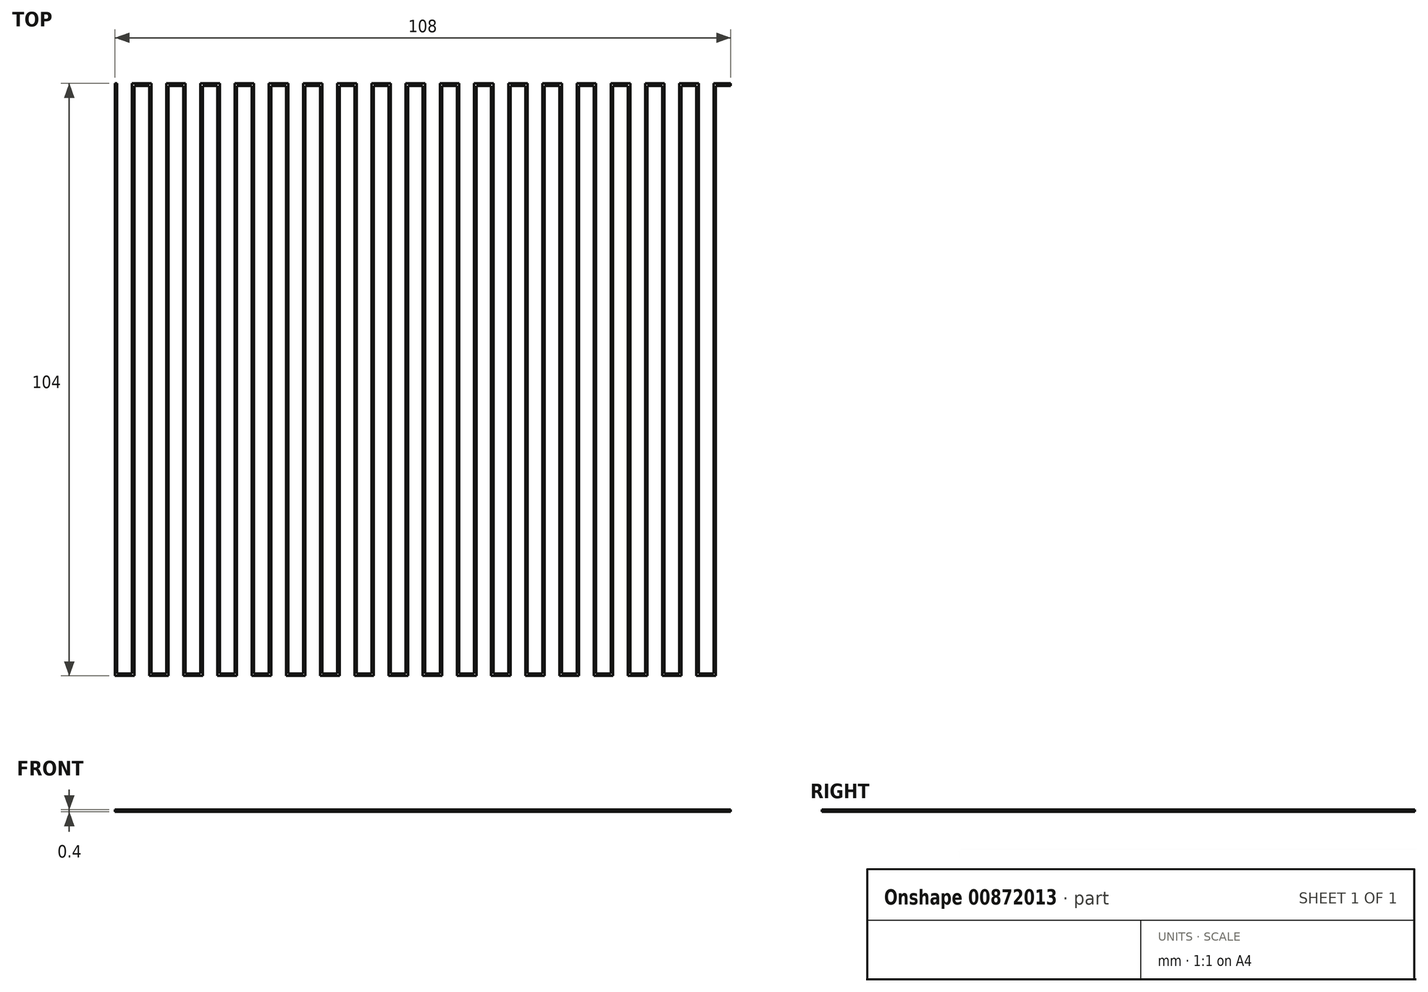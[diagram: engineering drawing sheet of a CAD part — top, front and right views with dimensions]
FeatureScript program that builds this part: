
annotation { "Feature Type Name" : "Feature", "Feature Type Description" : "" }
export const myFeature = defineFeature(function(context is Context, id is Id, definition is map)
    precondition{}
    {
        {
            var Q0;
            Q0=qCreatedBy(makeId("Top.planeOp"),FACE);
            var sketch = newSketch(context, id + "F0", { "sketchPlane" : qUnion([Q0])});
            skLineSegment(sketch, "E0.bottom", {"start": v(-52.6, 46.07) * mm, "end": v(-52.2, 46.07) * mm});
            skLineSegment(sketch, "E0.top", {"start": v(-52.6, -57.93) * mm, "end": v(-52.2, -57.93) * mm});
            skLineSegment(sketch, "E0.left", {"start": v(-52.6, 46.07) * mm, "end": v(-52.6, -57.93) * mm});
            skLineSegment(sketch, "E0.right", {"start": v(-52.2, 46.07) * mm, "end": v(-52.2, -57.93) * mm});
            skLineSegment(sketch, "E1.bottom", {"start": v(-52.6, -57.93) * mm, "end": v(-49.6, -57.93) * mm});
            skLineSegment(sketch, "E1.top", {"start": v(-52.6, -57.53) * mm, "end": v(-49.6, -57.53) * mm});
            skLineSegment(sketch, "E1.left", {"start": v(-52.6, -57.93) * mm, "end": v(-52.6, -57.53) * mm});
            skLineSegment(sketch, "E1.right", {"start": v(-49.6, -57.93) * mm, "end": v(-49.6, -57.53) * mm});
            skLineSegment(sketch, "E2.bottom", {"start": v(-49.6, -57.93) * mm, "end": v(-49.2, -57.93) * mm});
            skLineSegment(sketch, "E2.top", {"start": v(-49.6, 46.07) * mm, "end": v(-49.2, 46.07) * mm});
            skLineSegment(sketch, "E2.left", {"start": v(-49.6, -57.93) * mm, "end": v(-49.6, 46.07) * mm});
            skLineSegment(sketch, "E2.right", {"start": v(-49.2, -57.93) * mm, "end": v(-49.2, 46.07) * mm});
            skLineSegment(sketch, "E3.bottom", {"start": v(-49.6, 46.07) * mm, "end": v(-46.6, 46.07) * mm});
            skLineSegment(sketch, "E3.top", {"start": v(-49.6, 45.67) * mm, "end": v(-46.6, 45.67) * mm});
            skLineSegment(sketch, "E3.left", {"start": v(-49.6, 46.07) * mm, "end": v(-49.6, 45.67) * mm});
            skLineSegment(sketch, "E3.right", {"start": v(-46.6, 46.07) * mm, "end": v(-46.6, 45.67) * mm});
            skLineSegment(sketch, "E4.1.0.0", {"start": v(-46.2, 46.07) * mm, "end": v(-46.2, -57.93) * mm});
            skLineSegment(sketch, "E4.1.0.1", {"start": v(-46.6, 46.07) * mm, "end": v(-46.6, -57.93) * mm});
            skLineSegment(sketch, "E4.1.0.2", {"start": v(-43.2, -57.93) * mm, "end": v(-43.2, 46.07) * mm});
            skLineSegment(sketch, "E4.1.0.3", {"start": v(-43.6, -57.93) * mm, "end": v(-43.6, 46.07) * mm});
            skLineSegment(sketch, "E4.1.0.4", {"start": v(-43.6, 45.67) * mm, "end": v(-40.6, 45.67) * mm});
            skLineSegment(sketch, "E4.1.0.5", {"start": v(-46.6, 46.07) * mm, "end": v(-46.2, 46.07) * mm});
            skLineSegment(sketch, "E4.1.0.6", {"start": v(-43.6, 46.07) * mm, "end": v(-40.6, 46.07) * mm});
            skLineSegment(sketch, "E4.1.0.7", {"start": v(-40.6, 46.07) * mm, "end": v(-40.6, 45.67) * mm});
            skLineSegment(sketch, "E4.1.0.8", {"start": v(-46.6, -57.53) * mm, "end": v(-43.6, -57.53) * mm});
            skLineSegment(sketch, "E4.1.0.9", {"start": v(-46.6, -57.93) * mm, "end": v(-43.6, -57.93) * mm});
            skLineSegment(sketch, "E4.1.0.10", {"start": v(-46.6, -57.93) * mm, "end": v(-46.2, -57.93) * mm});
            skLineSegment(sketch, "E4.1.0.11", {"start": v(-46.6, -57.93) * mm, "end": v(-46.6, -57.53) * mm});
            skLineSegment(sketch, "E4.1.0.12", {"start": v(-43.6, -57.93) * mm, "end": v(-43.6, -57.53) * mm});
            skLineSegment(sketch, "E4.1.0.13", {"start": v(-43.6, -57.93) * mm, "end": v(-43.2, -57.93) * mm});
            skLineSegment(sketch, "E4.1.0.14", {"start": v(-43.6, 46.07) * mm, "end": v(-43.2, 46.07) * mm});
            skLineSegment(sketch, "E4.1.0.15", {"start": v(-43.6, 46.07) * mm, "end": v(-43.6, 45.67) * mm});
            skLineSegment(sketch, "E4.2.0.0", {"start": v(-40.2, 46.07) * mm, "end": v(-40.2, -57.93) * mm});
            skLineSegment(sketch, "E4.2.0.1", {"start": v(-40.6, 46.07) * mm, "end": v(-40.6, -57.93) * mm});
            skLineSegment(sketch, "E4.2.0.2", {"start": v(-37.2, -57.93) * mm, "end": v(-37.2, 46.07) * mm});
            skLineSegment(sketch, "E4.2.0.3", {"start": v(-37.6, -57.93) * mm, "end": v(-37.6, 46.07) * mm});
            skLineSegment(sketch, "E4.2.0.4", {"start": v(-37.6, 45.67) * mm, "end": v(-34.6, 45.67) * mm});
            skLineSegment(sketch, "E4.2.0.5", {"start": v(-40.6, 46.07) * mm, "end": v(-40.2, 46.07) * mm});
            skLineSegment(sketch, "E4.2.0.6", {"start": v(-37.6, 46.07) * mm, "end": v(-34.6, 46.07) * mm});
            skLineSegment(sketch, "E4.2.0.7", {"start": v(-34.6, 46.07) * mm, "end": v(-34.6, 45.67) * mm});
            skLineSegment(sketch, "E4.2.0.8", {"start": v(-40.6, -57.53) * mm, "end": v(-37.6, -57.53) * mm});
            skLineSegment(sketch, "E4.2.0.9", {"start": v(-40.6, -57.93) * mm, "end": v(-37.6, -57.93) * mm});
            skLineSegment(sketch, "E4.2.0.10", {"start": v(-40.6, -57.93) * mm, "end": v(-40.2, -57.93) * mm});
            skLineSegment(sketch, "E4.2.0.11", {"start": v(-40.6, -57.93) * mm, "end": v(-40.6, -57.53) * mm});
            skLineSegment(sketch, "E4.2.0.12", {"start": v(-37.6, -57.93) * mm, "end": v(-37.6, -57.53) * mm});
            skLineSegment(sketch, "E4.2.0.13", {"start": v(-37.6, -57.93) * mm, "end": v(-37.2, -57.93) * mm});
            skLineSegment(sketch, "E4.2.0.14", {"start": v(-37.6, 46.07) * mm, "end": v(-37.2, 46.07) * mm});
            skLineSegment(sketch, "E4.2.0.15", {"start": v(-37.6, 46.07) * mm, "end": v(-37.6, 45.67) * mm});
            skLineSegment(sketch, "E4.3.0.0", {"start": v(-34.2, 46.07) * mm, "end": v(-34.2, -57.93) * mm});
            skLineSegment(sketch, "E4.3.0.1", {"start": v(-34.6, 46.07) * mm, "end": v(-34.6, -57.93) * mm});
            skLineSegment(sketch, "E4.3.0.2", {"start": v(-31.2, -57.93) * mm, "end": v(-31.2, 46.07) * mm});
            skLineSegment(sketch, "E4.3.0.3", {"start": v(-31.6, -57.93) * mm, "end": v(-31.6, 46.07) * mm});
            skLineSegment(sketch, "E4.3.0.4", {"start": v(-31.6, 45.67) * mm, "end": v(-28.6, 45.67) * mm});
            skLineSegment(sketch, "E4.3.0.5", {"start": v(-34.6, 46.07) * mm, "end": v(-34.2, 46.07) * mm});
            skLineSegment(sketch, "E4.3.0.6", {"start": v(-31.6, 46.07) * mm, "end": v(-28.6, 46.07) * mm});
            skLineSegment(sketch, "E4.3.0.7", {"start": v(-28.6, 46.07) * mm, "end": v(-28.6, 45.67) * mm});
            skLineSegment(sketch, "E4.3.0.8", {"start": v(-34.6, -57.53) * mm, "end": v(-31.6, -57.53) * mm});
            skLineSegment(sketch, "E4.3.0.9", {"start": v(-34.6, -57.93) * mm, "end": v(-31.6, -57.93) * mm});
            skLineSegment(sketch, "E4.3.0.10", {"start": v(-34.6, -57.93) * mm, "end": v(-34.2, -57.93) * mm});
            skLineSegment(sketch, "E4.3.0.11", {"start": v(-34.6, -57.93) * mm, "end": v(-34.6, -57.53) * mm});
            skLineSegment(sketch, "E4.3.0.12", {"start": v(-31.6, -57.93) * mm, "end": v(-31.6, -57.53) * mm});
            skLineSegment(sketch, "E4.3.0.13", {"start": v(-31.6, -57.93) * mm, "end": v(-31.2, -57.93) * mm});
            skLineSegment(sketch, "E4.3.0.14", {"start": v(-31.6, 46.07) * mm, "end": v(-31.2, 46.07) * mm});
            skLineSegment(sketch, "E4.3.0.15", {"start": v(-31.6, 46.07) * mm, "end": v(-31.6, 45.67) * mm});
            skLineSegment(sketch, "E4.4.0.0", {"start": v(-28.2, 46.07) * mm, "end": v(-28.2, -57.93) * mm});
            skLineSegment(sketch, "E4.4.0.1", {"start": v(-28.6, 46.07) * mm, "end": v(-28.6, -57.93) * mm});
            skLineSegment(sketch, "E4.4.0.2", {"start": v(-25.2, -57.93) * mm, "end": v(-25.2, 46.07) * mm});
            skLineSegment(sketch, "E4.4.0.3", {"start": v(-25.6, -57.93) * mm, "end": v(-25.6, 46.07) * mm});
            skLineSegment(sketch, "E4.4.0.4", {"start": v(-25.6, 45.67) * mm, "end": v(-22.6, 45.67) * mm});
            skLineSegment(sketch, "E4.4.0.5", {"start": v(-28.6, 46.07) * mm, "end": v(-28.2, 46.07) * mm});
            skLineSegment(sketch, "E4.4.0.6", {"start": v(-25.6, 46.07) * mm, "end": v(-22.6, 46.07) * mm});
            skLineSegment(sketch, "E4.4.0.7", {"start": v(-22.6, 46.07) * mm, "end": v(-22.6, 45.67) * mm});
            skLineSegment(sketch, "E4.4.0.8", {"start": v(-28.6, -57.53) * mm, "end": v(-25.6, -57.53) * mm});
            skLineSegment(sketch, "E4.4.0.9", {"start": v(-28.6, -57.93) * mm, "end": v(-25.6, -57.93) * mm});
            skLineSegment(sketch, "E4.4.0.10", {"start": v(-28.6, -57.93) * mm, "end": v(-28.2, -57.93) * mm});
            skLineSegment(sketch, "E4.4.0.11", {"start": v(-28.6, -57.93) * mm, "end": v(-28.6, -57.53) * mm});
            skLineSegment(sketch, "E4.4.0.12", {"start": v(-25.6, -57.93) * mm, "end": v(-25.6, -57.53) * mm});
            skLineSegment(sketch, "E4.4.0.13", {"start": v(-25.6, -57.93) * mm, "end": v(-25.2, -57.93) * mm});
            skLineSegment(sketch, "E4.4.0.14", {"start": v(-25.6, 46.07) * mm, "end": v(-25.2, 46.07) * mm});
            skLineSegment(sketch, "E4.4.0.15", {"start": v(-25.6, 46.07) * mm, "end": v(-25.6, 45.67) * mm});
            skLineSegment(sketch, "E4.5.0.0", {"start": v(-22.2, 46.07) * mm, "end": v(-22.2, -57.93) * mm});
            skLineSegment(sketch, "E4.5.0.1", {"start": v(-22.6, 46.07) * mm, "end": v(-22.6, -57.93) * mm});
            skLineSegment(sketch, "E4.5.0.2", {"start": v(-19.2, -57.93) * mm, "end": v(-19.2, 46.07) * mm});
            skLineSegment(sketch, "E4.5.0.3", {"start": v(-19.6, -57.93) * mm, "end": v(-19.6, 46.07) * mm});
            skLineSegment(sketch, "E4.5.0.4", {"start": v(-19.6, 45.67) * mm, "end": v(-16.6, 45.67) * mm});
            skLineSegment(sketch, "E4.5.0.5", {"start": v(-22.6, 46.07) * mm, "end": v(-22.2, 46.07) * mm});
            skLineSegment(sketch, "E4.5.0.6", {"start": v(-19.6, 46.07) * mm, "end": v(-16.6, 46.07) * mm});
            skLineSegment(sketch, "E4.5.0.7", {"start": v(-16.6, 46.07) * mm, "end": v(-16.6, 45.67) * mm});
            skLineSegment(sketch, "E4.5.0.8", {"start": v(-22.6, -57.53) * mm, "end": v(-19.6, -57.53) * mm});
            skLineSegment(sketch, "E4.5.0.9", {"start": v(-22.6, -57.93) * mm, "end": v(-19.6, -57.93) * mm});
            skLineSegment(sketch, "E4.5.0.10", {"start": v(-22.6, -57.93) * mm, "end": v(-22.2, -57.93) * mm});
            skLineSegment(sketch, "E4.5.0.11", {"start": v(-22.6, -57.93) * mm, "end": v(-22.6, -57.53) * mm});
            skLineSegment(sketch, "E4.5.0.12", {"start": v(-19.6, -57.93) * mm, "end": v(-19.6, -57.53) * mm});
            skLineSegment(sketch, "E4.5.0.13", {"start": v(-19.6, -57.93) * mm, "end": v(-19.2, -57.93) * mm});
            skLineSegment(sketch, "E4.5.0.14", {"start": v(-19.6, 46.07) * mm, "end": v(-19.2, 46.07) * mm});
            skLineSegment(sketch, "E4.5.0.15", {"start": v(-19.6, 46.07) * mm, "end": v(-19.6, 45.67) * mm});
            skLineSegment(sketch, "E4.6.0.0", {"start": v(-16.2, 46.07) * mm, "end": v(-16.2, -57.93) * mm});
            skLineSegment(sketch, "E4.6.0.1", {"start": v(-16.6, 46.07) * mm, "end": v(-16.6, -57.93) * mm});
            skLineSegment(sketch, "E4.6.0.2", {"start": v(-13.2, -57.93) * mm, "end": v(-13.2, 46.07) * mm});
            skLineSegment(sketch, "E4.6.0.3", {"start": v(-13.6, -57.93) * mm, "end": v(-13.6, 46.07) * mm});
            skLineSegment(sketch, "E4.6.0.4", {"start": v(-13.6, 45.67) * mm, "end": v(-10.6, 45.67) * mm});
            skLineSegment(sketch, "E4.6.0.5", {"start": v(-16.6, 46.07) * mm, "end": v(-16.2, 46.07) * mm});
            skLineSegment(sketch, "E4.6.0.6", {"start": v(-13.6, 46.07) * mm, "end": v(-10.6, 46.07) * mm});
            skLineSegment(sketch, "E4.6.0.7", {"start": v(-10.6, 46.07) * mm, "end": v(-10.6, 45.67) * mm});
            skLineSegment(sketch, "E4.6.0.8", {"start": v(-16.6, -57.53) * mm, "end": v(-13.6, -57.53) * mm});
            skLineSegment(sketch, "E4.6.0.9", {"start": v(-16.6, -57.93) * mm, "end": v(-13.6, -57.93) * mm});
            skLineSegment(sketch, "E4.6.0.10", {"start": v(-16.6, -57.93) * mm, "end": v(-16.2, -57.93) * mm});
            skLineSegment(sketch, "E4.6.0.11", {"start": v(-16.6, -57.93) * mm, "end": v(-16.6, -57.53) * mm});
            skLineSegment(sketch, "E4.6.0.12", {"start": v(-13.6, -57.93) * mm, "end": v(-13.6, -57.53) * mm});
            skLineSegment(sketch, "E4.6.0.13", {"start": v(-13.6, -57.93) * mm, "end": v(-13.2, -57.93) * mm});
            skLineSegment(sketch, "E4.6.0.14", {"start": v(-13.6, 46.07) * mm, "end": v(-13.2, 46.07) * mm});
            skLineSegment(sketch, "E4.6.0.15", {"start": v(-13.6, 46.07) * mm, "end": v(-13.6, 45.67) * mm});
            skLineSegment(sketch, "E4.7.0.0", {"start": v(-10.2, 46.07) * mm, "end": v(-10.2, -57.93) * mm});
            skLineSegment(sketch, "E4.7.0.1", {"start": v(-10.6, 46.07) * mm, "end": v(-10.6, -57.93) * mm});
            skLineSegment(sketch, "E4.7.0.2", {"start": v(-7.2, -57.93) * mm, "end": v(-7.2, 46.07) * mm});
            skLineSegment(sketch, "E4.7.0.3", {"start": v(-7.6, -57.93) * mm, "end": v(-7.6, 46.07) * mm});
            skLineSegment(sketch, "E4.7.0.4", {"start": v(-7.6, 45.67) * mm, "end": v(-4.6, 45.67) * mm});
            skLineSegment(sketch, "E4.7.0.5", {"start": v(-10.6, 46.07) * mm, "end": v(-10.2, 46.07) * mm});
            skLineSegment(sketch, "E4.7.0.6", {"start": v(-7.6, 46.07) * mm, "end": v(-4.6, 46.07) * mm});
            skLineSegment(sketch, "E4.7.0.7", {"start": v(-4.6, 46.07) * mm, "end": v(-4.6, 45.67) * mm});
            skLineSegment(sketch, "E4.7.0.8", {"start": v(-10.6, -57.53) * mm, "end": v(-7.6, -57.53) * mm});
            skLineSegment(sketch, "E4.7.0.9", {"start": v(-10.6, -57.93) * mm, "end": v(-7.6, -57.93) * mm});
            skLineSegment(sketch, "E4.7.0.10", {"start": v(-10.6, -57.93) * mm, "end": v(-10.2, -57.93) * mm});
            skLineSegment(sketch, "E4.7.0.11", {"start": v(-10.6, -57.93) * mm, "end": v(-10.6, -57.53) * mm});
            skLineSegment(sketch, "E4.7.0.12", {"start": v(-7.6, -57.93) * mm, "end": v(-7.6, -57.53) * mm});
            skLineSegment(sketch, "E4.7.0.13", {"start": v(-7.6, -57.93) * mm, "end": v(-7.2, -57.93) * mm});
            skLineSegment(sketch, "E4.7.0.14", {"start": v(-7.6, 46.07) * mm, "end": v(-7.2, 46.07) * mm});
            skLineSegment(sketch, "E4.7.0.15", {"start": v(-7.6, 46.07) * mm, "end": v(-7.6, 45.67) * mm});
            skLineSegment(sketch, "E4.8.0.0", {"start": v(-4.2, 46.07) * mm, "end": v(-4.2, -57.93) * mm});
            skLineSegment(sketch, "E4.8.0.1", {"start": v(-4.6, 46.07) * mm, "end": v(-4.6, -57.93) * mm});
            skLineSegment(sketch, "E4.8.0.2", {"start": v(-1.2, -57.93) * mm, "end": v(-1.2, 46.07) * mm});
            skLineSegment(sketch, "E4.8.0.3", {"start": v(-1.6, -57.93) * mm, "end": v(-1.6, 46.07) * mm});
            skLineSegment(sketch, "E4.8.0.4", {"start": v(-1.6, 45.67) * mm, "end": v(1.4, 45.67) * mm});
            skLineSegment(sketch, "E4.8.0.5", {"start": v(-4.6, 46.07) * mm, "end": v(-4.2, 46.07) * mm});
            skLineSegment(sketch, "E4.8.0.6", {"start": v(-1.6, 46.07) * mm, "end": v(1.4, 46.07) * mm});
            skLineSegment(sketch, "E4.8.0.7", {"start": v(1.4, 46.07) * mm, "end": v(1.4, 45.67) * mm});
            skLineSegment(sketch, "E4.8.0.8", {"start": v(-4.6, -57.53) * mm, "end": v(-1.6, -57.53) * mm});
            skLineSegment(sketch, "E4.8.0.9", {"start": v(-4.6, -57.93) * mm, "end": v(-1.6, -57.93) * mm});
            skLineSegment(sketch, "E4.8.0.10", {"start": v(-4.6, -57.93) * mm, "end": v(-4.2, -57.93) * mm});
            skLineSegment(sketch, "E4.8.0.11", {"start": v(-4.6, -57.93) * mm, "end": v(-4.6, -57.53) * mm});
            skLineSegment(sketch, "E4.8.0.12", {"start": v(-1.6, -57.93) * mm, "end": v(-1.6, -57.53) * mm});
            skLineSegment(sketch, "E4.8.0.13", {"start": v(-1.6, -57.93) * mm, "end": v(-1.2, -57.93) * mm});
            skLineSegment(sketch, "E4.8.0.14", {"start": v(-1.6, 46.07) * mm, "end": v(-1.2, 46.07) * mm});
            skLineSegment(sketch, "E4.8.0.15", {"start": v(-1.6, 46.07) * mm, "end": v(-1.6, 45.67) * mm});
            skLineSegment(sketch, "E4.9.0.0", {"start": v(1.8, 46.07) * mm, "end": v(1.8, -57.93) * mm});
            skLineSegment(sketch, "E4.9.0.1", {"start": v(1.4, 46.07) * mm, "end": v(1.4, -57.93) * mm});
            skLineSegment(sketch, "E4.9.0.2", {"start": v(4.8, -57.93) * mm, "end": v(4.8, 46.07) * mm});
            skLineSegment(sketch, "E4.9.0.3", {"start": v(4.4, -57.93) * mm, "end": v(4.4, 46.07) * mm});
            skLineSegment(sketch, "E4.9.0.4", {"start": v(4.4, 45.67) * mm, "end": v(7.4, 45.67) * mm});
            skLineSegment(sketch, "E4.9.0.5", {"start": v(1.4, 46.07) * mm, "end": v(1.8, 46.07) * mm});
            skLineSegment(sketch, "E4.9.0.6", {"start": v(4.4, 46.07) * mm, "end": v(7.4, 46.07) * mm});
            skLineSegment(sketch, "E4.9.0.7", {"start": v(7.4, 46.07) * mm, "end": v(7.4, 45.67) * mm});
            skLineSegment(sketch, "E4.9.0.8", {"start": v(1.4, -57.53) * mm, "end": v(4.4, -57.53) * mm});
            skLineSegment(sketch, "E4.9.0.9", {"start": v(1.4, -57.93) * mm, "end": v(4.4, -57.93) * mm});
            skLineSegment(sketch, "E4.9.0.10", {"start": v(1.4, -57.93) * mm, "end": v(1.8, -57.93) * mm});
            skLineSegment(sketch, "E4.9.0.11", {"start": v(1.4, -57.93) * mm, "end": v(1.4, -57.53) * mm});
            skLineSegment(sketch, "E4.9.0.12", {"start": v(4.4, -57.93) * mm, "end": v(4.4, -57.53) * mm});
            skLineSegment(sketch, "E4.9.0.13", {"start": v(4.4, -57.93) * mm, "end": v(4.8, -57.93) * mm});
            skLineSegment(sketch, "E4.9.0.14", {"start": v(4.4, 46.07) * mm, "end": v(4.8, 46.07) * mm});
            skLineSegment(sketch, "E4.9.0.15", {"start": v(4.4, 46.07) * mm, "end": v(4.4, 45.67) * mm});
            skLineSegment(sketch, "E4.10.0.0", {"start": v(7.8, 46.07) * mm, "end": v(7.8, -57.93) * mm});
            skLineSegment(sketch, "E4.10.0.1", {"start": v(7.4, 46.07) * mm, "end": v(7.4, -57.93) * mm});
            skLineSegment(sketch, "E4.10.0.2", {"start": v(10.8, -57.93) * mm, "end": v(10.8, 46.07) * mm});
            skLineSegment(sketch, "E4.10.0.3", {"start": v(10.4, -57.93) * mm, "end": v(10.4, 46.07) * mm});
            skLineSegment(sketch, "E4.10.0.4", {"start": v(10.4, 45.67) * mm, "end": v(13.4, 45.67) * mm});
            skLineSegment(sketch, "E4.10.0.5", {"start": v(7.4, 46.07) * mm, "end": v(7.8, 46.07) * mm});
            skLineSegment(sketch, "E4.10.0.6", {"start": v(10.4, 46.07) * mm, "end": v(13.4, 46.07) * mm});
            skLineSegment(sketch, "E4.10.0.7", {"start": v(13.4, 46.07) * mm, "end": v(13.4, 45.67) * mm});
            skLineSegment(sketch, "E4.10.0.8", {"start": v(7.4, -57.53) * mm, "end": v(10.4, -57.53) * mm});
            skLineSegment(sketch, "E4.10.0.9", {"start": v(7.4, -57.93) * mm, "end": v(10.4, -57.93) * mm});
            skLineSegment(sketch, "E4.10.0.10", {"start": v(7.4, -57.93) * mm, "end": v(7.8, -57.93) * mm});
            skLineSegment(sketch, "E4.10.0.11", {"start": v(7.4, -57.93) * mm, "end": v(7.4, -57.53) * mm});
            skLineSegment(sketch, "E4.10.0.12", {"start": v(10.4, -57.93) * mm, "end": v(10.4, -57.53) * mm});
            skLineSegment(sketch, "E4.10.0.13", {"start": v(10.4, -57.93) * mm, "end": v(10.8, -57.93) * mm});
            skLineSegment(sketch, "E4.10.0.14", {"start": v(10.4, 46.07) * mm, "end": v(10.8, 46.07) * mm});
            skLineSegment(sketch, "E4.10.0.15", {"start": v(10.4, 46.07) * mm, "end": v(10.4, 45.67) * mm});
            skLineSegment(sketch, "E4.11.0.0", {"start": v(13.8, 46.07) * mm, "end": v(13.8, -57.93) * mm});
            skLineSegment(sketch, "E4.11.0.1", {"start": v(13.4, 46.07) * mm, "end": v(13.4, -57.93) * mm});
            skLineSegment(sketch, "E4.11.0.2", {"start": v(16.8, -57.93) * mm, "end": v(16.8, 46.07) * mm});
            skLineSegment(sketch, "E4.11.0.3", {"start": v(16.4, -57.93) * mm, "end": v(16.4, 46.07) * mm});
            skLineSegment(sketch, "E4.11.0.4", {"start": v(16.4, 45.67) * mm, "end": v(19.4, 45.67) * mm});
            skLineSegment(sketch, "E4.11.0.5", {"start": v(13.4, 46.07) * mm, "end": v(13.8, 46.07) * mm});
            skLineSegment(sketch, "E4.11.0.6", {"start": v(16.4, 46.07) * mm, "end": v(19.4, 46.07) * mm});
            skLineSegment(sketch, "E4.11.0.7", {"start": v(19.4, 46.07) * mm, "end": v(19.4, 45.67) * mm});
            skLineSegment(sketch, "E4.11.0.8", {"start": v(13.4, -57.53) * mm, "end": v(16.4, -57.53) * mm});
            skLineSegment(sketch, "E4.11.0.9", {"start": v(13.4, -57.93) * mm, "end": v(16.4, -57.93) * mm});
            skLineSegment(sketch, "E4.11.0.10", {"start": v(13.4, -57.93) * mm, "end": v(13.8, -57.93) * mm});
            skLineSegment(sketch, "E4.11.0.11", {"start": v(13.4, -57.93) * mm, "end": v(13.4, -57.53) * mm});
            skLineSegment(sketch, "E4.11.0.12", {"start": v(16.4, -57.93) * mm, "end": v(16.4, -57.53) * mm});
            skLineSegment(sketch, "E4.11.0.13", {"start": v(16.4, -57.93) * mm, "end": v(16.8, -57.93) * mm});
            skLineSegment(sketch, "E4.11.0.14", {"start": v(16.4, 46.07) * mm, "end": v(16.8, 46.07) * mm});
            skLineSegment(sketch, "E4.11.0.15", {"start": v(16.4, 46.07) * mm, "end": v(16.4, 45.67) * mm});
            skLineSegment(sketch, "E4.12.0.0", {"start": v(19.8, 46.07) * mm, "end": v(19.8, -57.93) * mm});
            skLineSegment(sketch, "E4.12.0.1", {"start": v(19.4, 46.07) * mm, "end": v(19.4, -57.93) * mm});
            skLineSegment(sketch, "E4.12.0.2", {"start": v(22.8, -57.93) * mm, "end": v(22.8, 46.07) * mm});
            skLineSegment(sketch, "E4.12.0.3", {"start": v(22.4, -57.93) * mm, "end": v(22.4, 46.07) * mm});
            skLineSegment(sketch, "E4.12.0.4", {"start": v(22.4, 45.67) * mm, "end": v(25.4, 45.67) * mm});
            skLineSegment(sketch, "E4.12.0.5", {"start": v(19.4, 46.07) * mm, "end": v(19.8, 46.07) * mm});
            skLineSegment(sketch, "E4.12.0.6", {"start": v(22.4, 46.07) * mm, "end": v(25.4, 46.07) * mm});
            skLineSegment(sketch, "E4.12.0.7", {"start": v(25.4, 46.07) * mm, "end": v(25.4, 45.67) * mm});
            skLineSegment(sketch, "E4.12.0.8", {"start": v(19.4, -57.53) * mm, "end": v(22.4, -57.53) * mm});
            skLineSegment(sketch, "E4.12.0.9", {"start": v(19.4, -57.93) * mm, "end": v(22.4, -57.93) * mm});
            skLineSegment(sketch, "E4.12.0.10", {"start": v(19.4, -57.93) * mm, "end": v(19.8, -57.93) * mm});
            skLineSegment(sketch, "E4.12.0.11", {"start": v(19.4, -57.93) * mm, "end": v(19.4, -57.53) * mm});
            skLineSegment(sketch, "E4.12.0.12", {"start": v(22.4, -57.93) * mm, "end": v(22.4, -57.53) * mm});
            skLineSegment(sketch, "E4.12.0.13", {"start": v(22.4, -57.93) * mm, "end": v(22.8, -57.93) * mm});
            skLineSegment(sketch, "E4.12.0.14", {"start": v(22.4, 46.07) * mm, "end": v(22.8, 46.07) * mm});
            skLineSegment(sketch, "E4.12.0.15", {"start": v(22.4, 46.07) * mm, "end": v(22.4, 45.67) * mm});
            skLineSegment(sketch, "E4.13.0.0", {"start": v(25.8, 46.07) * mm, "end": v(25.8, -57.93) * mm});
            skLineSegment(sketch, "E4.13.0.1", {"start": v(25.4, 46.07) * mm, "end": v(25.4, -57.93) * mm});
            skLineSegment(sketch, "E4.13.0.2", {"start": v(28.8, -57.93) * mm, "end": v(28.8, 46.07) * mm});
            skLineSegment(sketch, "E4.13.0.3", {"start": v(28.4, -57.93) * mm, "end": v(28.4, 46.07) * mm});
            skLineSegment(sketch, "E4.13.0.4", {"start": v(28.4, 45.67) * mm, "end": v(31.4, 45.67) * mm});
            skLineSegment(sketch, "E4.13.0.5", {"start": v(25.4, 46.07) * mm, "end": v(25.8, 46.07) * mm});
            skLineSegment(sketch, "E4.13.0.6", {"start": v(28.4, 46.07) * mm, "end": v(31.4, 46.07) * mm});
            skLineSegment(sketch, "E4.13.0.7", {"start": v(31.4, 46.07) * mm, "end": v(31.4, 45.67) * mm});
            skLineSegment(sketch, "E4.13.0.8", {"start": v(25.4, -57.53) * mm, "end": v(28.4, -57.53) * mm});
            skLineSegment(sketch, "E4.13.0.9", {"start": v(25.4, -57.93) * mm, "end": v(28.4, -57.93) * mm});
            skLineSegment(sketch, "E4.13.0.10", {"start": v(25.4, -57.93) * mm, "end": v(25.8, -57.93) * mm});
            skLineSegment(sketch, "E4.13.0.11", {"start": v(25.4, -57.93) * mm, "end": v(25.4, -57.53) * mm});
            skLineSegment(sketch, "E4.13.0.12", {"start": v(28.4, -57.93) * mm, "end": v(28.4, -57.53) * mm});
            skLineSegment(sketch, "E4.13.0.13", {"start": v(28.4, -57.93) * mm, "end": v(28.8, -57.93) * mm});
            skLineSegment(sketch, "E4.13.0.14", {"start": v(28.4, 46.07) * mm, "end": v(28.8, 46.07) * mm});
            skLineSegment(sketch, "E4.13.0.15", {"start": v(28.4, 46.07) * mm, "end": v(28.4, 45.67) * mm});
            skLineSegment(sketch, "E4.14.0.0", {"start": v(31.8, 46.07) * mm, "end": v(31.8, -57.93) * mm});
            skLineSegment(sketch, "E4.14.0.1", {"start": v(31.4, 46.07) * mm, "end": v(31.4, -57.93) * mm});
            skLineSegment(sketch, "E4.14.0.2", {"start": v(34.8, -57.93) * mm, "end": v(34.8, 46.07) * mm});
            skLineSegment(sketch, "E4.14.0.3", {"start": v(34.4, -57.93) * mm, "end": v(34.4, 46.07) * mm});
            skLineSegment(sketch, "E4.14.0.4", {"start": v(34.4, 45.67) * mm, "end": v(37.4, 45.67) * mm});
            skLineSegment(sketch, "E4.14.0.5", {"start": v(31.4, 46.07) * mm, "end": v(31.8, 46.07) * mm});
            skLineSegment(sketch, "E4.14.0.6", {"start": v(34.4, 46.07) * mm, "end": v(37.4, 46.07) * mm});
            skLineSegment(sketch, "E4.14.0.7", {"start": v(37.4, 46.07) * mm, "end": v(37.4, 45.67) * mm});
            skLineSegment(sketch, "E4.14.0.8", {"start": v(31.4, -57.53) * mm, "end": v(34.4, -57.53) * mm});
            skLineSegment(sketch, "E4.14.0.9", {"start": v(31.4, -57.93) * mm, "end": v(34.4, -57.93) * mm});
            skLineSegment(sketch, "E4.14.0.10", {"start": v(31.4, -57.93) * mm, "end": v(31.8, -57.93) * mm});
            skLineSegment(sketch, "E4.14.0.11", {"start": v(31.4, -57.93) * mm, "end": v(31.4, -57.53) * mm});
            skLineSegment(sketch, "E4.14.0.12", {"start": v(34.4, -57.93) * mm, "end": v(34.4, -57.53) * mm});
            skLineSegment(sketch, "E4.14.0.13", {"start": v(34.4, -57.93) * mm, "end": v(34.8, -57.93) * mm});
            skLineSegment(sketch, "E4.14.0.14", {"start": v(34.4, 46.07) * mm, "end": v(34.8, 46.07) * mm});
            skLineSegment(sketch, "E4.14.0.15", {"start": v(34.4, 46.07) * mm, "end": v(34.4, 45.67) * mm});
            skLineSegment(sketch, "E4.15.0.0", {"start": v(37.8, 46.07) * mm, "end": v(37.8, -57.93) * mm});
            skLineSegment(sketch, "E4.15.0.1", {"start": v(37.4, 46.07) * mm, "end": v(37.4, -57.93) * mm});
            skLineSegment(sketch, "E4.15.0.2", {"start": v(40.8, -57.93) * mm, "end": v(40.8, 46.07) * mm});
            skLineSegment(sketch, "E4.15.0.3", {"start": v(40.4, -57.93) * mm, "end": v(40.4, 46.07) * mm});
            skLineSegment(sketch, "E4.15.0.4", {"start": v(40.4, 45.67) * mm, "end": v(43.4, 45.67) * mm});
            skLineSegment(sketch, "E4.15.0.5", {"start": v(37.4, 46.07) * mm, "end": v(37.8, 46.07) * mm});
            skLineSegment(sketch, "E4.15.0.6", {"start": v(40.4, 46.07) * mm, "end": v(43.4, 46.07) * mm});
            skLineSegment(sketch, "E4.15.0.7", {"start": v(43.4, 46.07) * mm, "end": v(43.4, 45.67) * mm});
            skLineSegment(sketch, "E4.15.0.8", {"start": v(37.4, -57.53) * mm, "end": v(40.4, -57.53) * mm});
            skLineSegment(sketch, "E4.15.0.9", {"start": v(37.4, -57.93) * mm, "end": v(40.4, -57.93) * mm});
            skLineSegment(sketch, "E4.15.0.10", {"start": v(37.4, -57.93) * mm, "end": v(37.8, -57.93) * mm});
            skLineSegment(sketch, "E4.15.0.11", {"start": v(37.4, -57.93) * mm, "end": v(37.4, -57.53) * mm});
            skLineSegment(sketch, "E4.15.0.12", {"start": v(40.4, -57.93) * mm, "end": v(40.4, -57.53) * mm});
            skLineSegment(sketch, "E4.15.0.13", {"start": v(40.4, -57.93) * mm, "end": v(40.8, -57.93) * mm});
            skLineSegment(sketch, "E4.15.0.14", {"start": v(40.4, 46.07) * mm, "end": v(40.8, 46.07) * mm});
            skLineSegment(sketch, "E4.15.0.15", {"start": v(40.4, 46.07) * mm, "end": v(40.4, 45.67) * mm});
            skLineSegment(sketch, "E4.16.0.0", {"start": v(43.8, 46.07) * mm, "end": v(43.8, -57.93) * mm});
            skLineSegment(sketch, "E4.16.0.1", {"start": v(43.4, 46.07) * mm, "end": v(43.4, -57.93) * mm});
            skLineSegment(sketch, "E4.16.0.2", {"start": v(46.8, -57.93) * mm, "end": v(46.8, 46.07) * mm});
            skLineSegment(sketch, "E4.16.0.3", {"start": v(46.4, -57.93) * mm, "end": v(46.4, 46.07) * mm});
            skLineSegment(sketch, "E4.16.0.4", {"start": v(46.4, 45.67) * mm, "end": v(49.4, 45.67) * mm});
            skLineSegment(sketch, "E4.16.0.5", {"start": v(43.4, 46.07) * mm, "end": v(43.8, 46.07) * mm});
            skLineSegment(sketch, "E4.16.0.6", {"start": v(46.4, 46.07) * mm, "end": v(49.4, 46.07) * mm});
            skLineSegment(sketch, "E4.16.0.7", {"start": v(49.4, 46.07) * mm, "end": v(49.4, 45.67) * mm});
            skLineSegment(sketch, "E4.16.0.8", {"start": v(43.4, -57.53) * mm, "end": v(46.4, -57.53) * mm});
            skLineSegment(sketch, "E4.16.0.9", {"start": v(43.4, -57.93) * mm, "end": v(46.4, -57.93) * mm});
            skLineSegment(sketch, "E4.16.0.10", {"start": v(43.4, -57.93) * mm, "end": v(43.8, -57.93) * mm});
            skLineSegment(sketch, "E4.16.0.11", {"start": v(43.4, -57.93) * mm, "end": v(43.4, -57.53) * mm});
            skLineSegment(sketch, "E4.16.0.12", {"start": v(46.4, -57.93) * mm, "end": v(46.4, -57.53) * mm});
            skLineSegment(sketch, "E4.16.0.13", {"start": v(46.4, -57.93) * mm, "end": v(46.8, -57.93) * mm});
            skLineSegment(sketch, "E4.16.0.14", {"start": v(46.4, 46.07) * mm, "end": v(46.8, 46.07) * mm});
            skLineSegment(sketch, "E4.16.0.15", {"start": v(46.4, 46.07) * mm, "end": v(46.4, 45.67) * mm});
            skLineSegment(sketch, "E4.17.0.0", {"start": v(49.8, 46.07) * mm, "end": v(49.8, -57.93) * mm});
            skLineSegment(sketch, "E4.17.0.1", {"start": v(49.4, 46.07) * mm, "end": v(49.4, -57.93) * mm});
            skLineSegment(sketch, "E4.17.0.2", {"start": v(52.8, -57.93) * mm, "end": v(52.8, 46.07) * mm});
            skLineSegment(sketch, "E4.17.0.3", {"start": v(52.4, -57.93) * mm, "end": v(52.4, 46.07) * mm});
            skLineSegment(sketch, "E4.17.0.4", {"start": v(52.4, 45.67) * mm, "end": v(55.4, 45.67) * mm});
            skLineSegment(sketch, "E4.17.0.5", {"start": v(49.4, 46.07) * mm, "end": v(49.8, 46.07) * mm});
            skLineSegment(sketch, "E4.17.0.6", {"start": v(52.4, 46.07) * mm, "end": v(55.4, 46.07) * mm});
            skLineSegment(sketch, "E4.17.0.7", {"start": v(55.4, 46.07) * mm, "end": v(55.4, 45.67) * mm});
            skLineSegment(sketch, "E4.17.0.8", {"start": v(49.4, -57.53) * mm, "end": v(52.4, -57.53) * mm});
            skLineSegment(sketch, "E4.17.0.9", {"start": v(49.4, -57.93) * mm, "end": v(52.4, -57.93) * mm});
            skLineSegment(sketch, "E4.17.0.10", {"start": v(49.4, -57.93) * mm, "end": v(49.8, -57.93) * mm});
            skLineSegment(sketch, "E4.17.0.11", {"start": v(49.4, -57.93) * mm, "end": v(49.4, -57.53) * mm});
            skLineSegment(sketch, "E4.17.0.12", {"start": v(52.4, -57.93) * mm, "end": v(52.4, -57.53) * mm});
            skLineSegment(sketch, "E4.17.0.13", {"start": v(52.4, -57.93) * mm, "end": v(52.8, -57.93) * mm});
            skLineSegment(sketch, "E4.17.0.14", {"start": v(52.4, 46.07) * mm, "end": v(52.8, 46.07) * mm});
            skLineSegment(sketch, "E4.17.0.15", {"start": v(52.4, 46.07) * mm, "end": v(52.4, 45.67) * mm});
            skLineSegment(sketch, "E4.direction1", {"start": v(-52.6, -57.93) * mm, "end": v(-46.6, -57.93) * mm, "construction": true});
            skSolve(sketch);
        }
        {
            var Q0;
            {var subQ0=sQuery(id+"F0.wireOp",EDGE,"E4.17.0.6");var subQ1=sQuery(id+"F0.wireOp",EDGE,"E4.17.0.2");var subQ2=makeQuery(id+"F0.imprint","INTERSECT",VERTEX,{"derivedFrom":[subQ1,subQ0]});var subQ5=makeQuery(id+"F0.imprint","IMPRINT",EDGE,{"disambiguationData":[TD([[subQ2,1.0]])],"derivedFrom":subQ1});var subQ12=sQuery(id+"F0.wireOp",EDGE,"E4.17.0.13");var subQ13=sQuery(id+"F0.wireOp",EDGE,"E4.17.0.9");var subQ16=sQuery(id+"F0.wireOp",EDGE,"E4.17.0.0");var subQ17=makeQuery(id+"F0.imprint","INTERSECT",VERTEX,{"derivedFrom":[subQ16,subQ13]});var subQ19=makeQuery(id+"F0.imprint","IMPRINT",EDGE,{"disambiguationData":[TD([[subQ17,1.0]])],"derivedFrom":subQ16});var subQ25=sQuery(id+"F0.wireOp",EDGE,"E4.16.0.7");var subQ28=makeQuery(id+"F0.imprint","IMPRINT",EDGE,{"derivedFrom":subQ25});var subQ29=sQuery(id+"F0.wireOp",EDGE,"E4.16.0.6");var subQ30=sQuery(id+"F0.wireOp",EDGE,"E4.16.0.2");var subQ31=makeQuery(id+"F0.imprint","INTERSECT",VERTEX,{"derivedFrom":[subQ30,subQ29]});var subQ33=makeQuery(id+"F0.imprint","IMPRINT",EDGE,{"disambiguationData":[TD([[subQ31,1.0]])],"derivedFrom":subQ30});var subQ40=sQuery(id+"F0.wireOp",EDGE,"E4.16.0.13");var subQ41=sQuery(id+"F0.wireOp",EDGE,"E4.16.0.9");var subQ44=sQuery(id+"F0.wireOp",EDGE,"E4.16.0.0");var subQ45=makeQuery(id+"F0.imprint","INTERSECT",VERTEX,{"derivedFrom":[subQ44,subQ41]});var subQ47=makeQuery(id+"F0.imprint","IMPRINT",EDGE,{"disambiguationData":[TD([[subQ45,1.0]])],"derivedFrom":subQ44});var subQ53=sQuery(id+"F0.wireOp",EDGE,"E4.15.0.7");var subQ56=makeQuery(id+"F0.imprint","IMPRINT",EDGE,{"derivedFrom":subQ53});var subQ57=sQuery(id+"F0.wireOp",EDGE,"E4.15.0.6");var subQ58=sQuery(id+"F0.wireOp",EDGE,"E4.15.0.2");var subQ59=makeQuery(id+"F0.imprint","INTERSECT",VERTEX,{"derivedFrom":[subQ58,subQ57]});var subQ61=makeQuery(id+"F0.imprint","IMPRINT",EDGE,{"disambiguationData":[TD([[subQ59,1.0]])],"derivedFrom":subQ58});var subQ68=sQuery(id+"F0.wireOp",EDGE,"E4.15.0.13");var subQ69=sQuery(id+"F0.wireOp",EDGE,"E4.15.0.9");var subQ72=sQuery(id+"F0.wireOp",EDGE,"E4.15.0.0");var subQ73=makeQuery(id+"F0.imprint","INTERSECT",VERTEX,{"derivedFrom":[subQ72,subQ69]});var subQ75=makeQuery(id+"F0.imprint","IMPRINT",EDGE,{"disambiguationData":[TD([[subQ73,1.0]])],"derivedFrom":subQ72});var subQ81=sQuery(id+"F0.wireOp",EDGE,"E4.14.0.7");var subQ84=makeQuery(id+"F0.imprint","IMPRINT",EDGE,{"derivedFrom":subQ81});var subQ85=sQuery(id+"F0.wireOp",EDGE,"E4.14.0.6");var subQ86=sQuery(id+"F0.wireOp",EDGE,"E4.14.0.2");var subQ87=makeQuery(id+"F0.imprint","INTERSECT",VERTEX,{"derivedFrom":[subQ86,subQ85]});var subQ89=makeQuery(id+"F0.imprint","IMPRINT",EDGE,{"disambiguationData":[TD([[subQ87,1.0]])],"derivedFrom":subQ86});var subQ96=sQuery(id+"F0.wireOp",EDGE,"E4.14.0.13");var subQ97=sQuery(id+"F0.wireOp",EDGE,"E4.14.0.9");var subQ100=sQuery(id+"F0.wireOp",EDGE,"E4.14.0.0");var subQ101=makeQuery(id+"F0.imprint","INTERSECT",VERTEX,{"derivedFrom":[subQ100,subQ97]});var subQ103=makeQuery(id+"F0.imprint","IMPRINT",EDGE,{"disambiguationData":[TD([[subQ101,1.0]])],"derivedFrom":subQ100});var subQ109=sQuery(id+"F0.wireOp",EDGE,"E4.13.0.7");var subQ112=makeQuery(id+"F0.imprint","IMPRINT",EDGE,{"derivedFrom":subQ109});var subQ113=sQuery(id+"F0.wireOp",EDGE,"E4.13.0.6");var subQ114=sQuery(id+"F0.wireOp",EDGE,"E4.13.0.2");var subQ115=makeQuery(id+"F0.imprint","INTERSECT",VERTEX,{"derivedFrom":[subQ114,subQ113]});var subQ117=makeQuery(id+"F0.imprint","IMPRINT",EDGE,{"disambiguationData":[TD([[subQ115,1.0]])],"derivedFrom":subQ114});var subQ124=sQuery(id+"F0.wireOp",EDGE,"E4.13.0.13");var subQ125=sQuery(id+"F0.wireOp",EDGE,"E4.13.0.9");var subQ128=sQuery(id+"F0.wireOp",EDGE,"E4.13.0.0");var subQ129=makeQuery(id+"F0.imprint","INTERSECT",VERTEX,{"derivedFrom":[subQ128,subQ125]});var subQ131=makeQuery(id+"F0.imprint","IMPRINT",EDGE,{"disambiguationData":[TD([[subQ129,1.0]])],"derivedFrom":subQ128});var subQ137=sQuery(id+"F0.wireOp",EDGE,"E4.12.0.7");var subQ140=makeQuery(id+"F0.imprint","IMPRINT",EDGE,{"derivedFrom":subQ137});var subQ141=sQuery(id+"F0.wireOp",EDGE,"E4.12.0.6");var subQ142=sQuery(id+"F0.wireOp",EDGE,"E4.12.0.2");var subQ143=makeQuery(id+"F0.imprint","INTERSECT",VERTEX,{"derivedFrom":[subQ142,subQ141]});var subQ145=makeQuery(id+"F0.imprint","IMPRINT",EDGE,{"disambiguationData":[TD([[subQ143,1.0]])],"derivedFrom":subQ142});var subQ152=sQuery(id+"F0.wireOp",EDGE,"E4.12.0.13");var subQ153=sQuery(id+"F0.wireOp",EDGE,"E4.12.0.9");var subQ156=sQuery(id+"F0.wireOp",EDGE,"E4.12.0.0");var subQ157=makeQuery(id+"F0.imprint","INTERSECT",VERTEX,{"derivedFrom":[subQ156,subQ153]});var subQ159=makeQuery(id+"F0.imprint","IMPRINT",EDGE,{"disambiguationData":[TD([[subQ157,1.0]])],"derivedFrom":subQ156});var subQ165=sQuery(id+"F0.wireOp",EDGE,"E4.11.0.7");var subQ168=makeQuery(id+"F0.imprint","IMPRINT",EDGE,{"derivedFrom":subQ165});var subQ169=sQuery(id+"F0.wireOp",EDGE,"E4.11.0.6");var subQ170=sQuery(id+"F0.wireOp",EDGE,"E4.11.0.2");var subQ171=makeQuery(id+"F0.imprint","INTERSECT",VERTEX,{"derivedFrom":[subQ170,subQ169]});var subQ173=makeQuery(id+"F0.imprint","IMPRINT",EDGE,{"disambiguationData":[TD([[subQ171,1.0]])],"derivedFrom":subQ170});var subQ180=sQuery(id+"F0.wireOp",EDGE,"E4.11.0.13");var subQ181=sQuery(id+"F0.wireOp",EDGE,"E4.11.0.9");var subQ184=sQuery(id+"F0.wireOp",EDGE,"E4.11.0.0");var subQ185=makeQuery(id+"F0.imprint","INTERSECT",VERTEX,{"derivedFrom":[subQ184,subQ181]});var subQ187=makeQuery(id+"F0.imprint","IMPRINT",EDGE,{"disambiguationData":[TD([[subQ185,1.0]])],"derivedFrom":subQ184});var subQ193=sQuery(id+"F0.wireOp",EDGE,"E4.10.0.7");var subQ196=makeQuery(id+"F0.imprint","IMPRINT",EDGE,{"derivedFrom":subQ193});var subQ197=sQuery(id+"F0.wireOp",EDGE,"E4.10.0.6");var subQ198=sQuery(id+"F0.wireOp",EDGE,"E4.10.0.2");var subQ199=makeQuery(id+"F0.imprint","INTERSECT",VERTEX,{"derivedFrom":[subQ198,subQ197]});var subQ201=makeQuery(id+"F0.imprint","IMPRINT",EDGE,{"disambiguationData":[TD([[subQ199,1.0]])],"derivedFrom":subQ198});var subQ208=sQuery(id+"F0.wireOp",EDGE,"E4.10.0.13");var subQ209=sQuery(id+"F0.wireOp",EDGE,"E4.10.0.9");var subQ212=sQuery(id+"F0.wireOp",EDGE,"E4.10.0.0");var subQ213=makeQuery(id+"F0.imprint","INTERSECT",VERTEX,{"derivedFrom":[subQ212,subQ209]});var subQ215=makeQuery(id+"F0.imprint","IMPRINT",EDGE,{"disambiguationData":[TD([[subQ213,1.0]])],"derivedFrom":subQ212});var subQ221=sQuery(id+"F0.wireOp",EDGE,"E4.9.0.7");var subQ224=makeQuery(id+"F0.imprint","IMPRINT",EDGE,{"derivedFrom":subQ221});var subQ225=sQuery(id+"F0.wireOp",EDGE,"E4.9.0.6");var subQ226=sQuery(id+"F0.wireOp",EDGE,"E4.9.0.2");var subQ227=makeQuery(id+"F0.imprint","INTERSECT",VERTEX,{"derivedFrom":[subQ226,subQ225]});var subQ229=makeQuery(id+"F0.imprint","IMPRINT",EDGE,{"disambiguationData":[TD([[subQ227,1.0]])],"derivedFrom":subQ226});var subQ236=sQuery(id+"F0.wireOp",EDGE,"E4.9.0.13");var subQ237=sQuery(id+"F0.wireOp",EDGE,"E4.9.0.9");var subQ240=sQuery(id+"F0.wireOp",EDGE,"E4.9.0.0");var subQ241=makeQuery(id+"F0.imprint","INTERSECT",VERTEX,{"derivedFrom":[subQ240,subQ237]});var subQ243=makeQuery(id+"F0.imprint","IMPRINT",EDGE,{"disambiguationData":[TD([[subQ241,1.0]])],"derivedFrom":subQ240});var subQ249=sQuery(id+"F0.wireOp",EDGE,"E4.8.0.7");var subQ252=makeQuery(id+"F0.imprint","IMPRINT",EDGE,{"derivedFrom":subQ249});var subQ253=sQuery(id+"F0.wireOp",EDGE,"E4.8.0.6");var subQ254=sQuery(id+"F0.wireOp",EDGE,"E4.8.0.2");var subQ255=makeQuery(id+"F0.imprint","INTERSECT",VERTEX,{"derivedFrom":[subQ254,subQ253]});var subQ257=makeQuery(id+"F0.imprint","IMPRINT",EDGE,{"disambiguationData":[TD([[subQ255,1.0]])],"derivedFrom":subQ254});var subQ264=sQuery(id+"F0.wireOp",EDGE,"E4.8.0.13");var subQ265=sQuery(id+"F0.wireOp",EDGE,"E4.8.0.9");var subQ268=sQuery(id+"F0.wireOp",EDGE,"E4.8.0.0");var subQ269=makeQuery(id+"F0.imprint","INTERSECT",VERTEX,{"derivedFrom":[subQ268,subQ265]});var subQ271=makeQuery(id+"F0.imprint","IMPRINT",EDGE,{"disambiguationData":[TD([[subQ269,1.0]])],"derivedFrom":subQ268});var subQ277=sQuery(id+"F0.wireOp",EDGE,"E4.7.0.7");var subQ280=makeQuery(id+"F0.imprint","IMPRINT",EDGE,{"derivedFrom":subQ277});var subQ281=sQuery(id+"F0.wireOp",EDGE,"E4.7.0.6");var subQ282=sQuery(id+"F0.wireOp",EDGE,"E4.7.0.2");var subQ283=makeQuery(id+"F0.imprint","INTERSECT",VERTEX,{"derivedFrom":[subQ282,subQ281]});var subQ285=makeQuery(id+"F0.imprint","IMPRINT",EDGE,{"disambiguationData":[TD([[subQ283,1.0]])],"derivedFrom":subQ282});var subQ292=sQuery(id+"F0.wireOp",EDGE,"E4.7.0.13");var subQ293=sQuery(id+"F0.wireOp",EDGE,"E4.7.0.9");var subQ296=sQuery(id+"F0.wireOp",EDGE,"E4.7.0.0");var subQ297=makeQuery(id+"F0.imprint","INTERSECT",VERTEX,{"derivedFrom":[subQ296,subQ293]});var subQ299=makeQuery(id+"F0.imprint","IMPRINT",EDGE,{"disambiguationData":[TD([[subQ297,1.0]])],"derivedFrom":subQ296});var subQ305=sQuery(id+"F0.wireOp",EDGE,"E4.6.0.7");var subQ308=makeQuery(id+"F0.imprint","IMPRINT",EDGE,{"derivedFrom":subQ305});var subQ309=sQuery(id+"F0.wireOp",EDGE,"E4.6.0.6");var subQ310=sQuery(id+"F0.wireOp",EDGE,"E4.6.0.2");var subQ311=makeQuery(id+"F0.imprint","INTERSECT",VERTEX,{"derivedFrom":[subQ310,subQ309]});var subQ313=makeQuery(id+"F0.imprint","IMPRINT",EDGE,{"disambiguationData":[TD([[subQ311,1.0]])],"derivedFrom":subQ310});var subQ320=sQuery(id+"F0.wireOp",EDGE,"E4.6.0.13");var subQ321=sQuery(id+"F0.wireOp",EDGE,"E4.6.0.9");var subQ324=sQuery(id+"F0.wireOp",EDGE,"E4.6.0.0");var subQ325=makeQuery(id+"F0.imprint","INTERSECT",VERTEX,{"derivedFrom":[subQ324,subQ321]});var subQ327=makeQuery(id+"F0.imprint","IMPRINT",EDGE,{"disambiguationData":[TD([[subQ325,1.0]])],"derivedFrom":subQ324});var subQ333=sQuery(id+"F0.wireOp",EDGE,"E4.5.0.7");var subQ336=makeQuery(id+"F0.imprint","IMPRINT",EDGE,{"derivedFrom":subQ333});var subQ337=sQuery(id+"F0.wireOp",EDGE,"E4.5.0.6");var subQ338=sQuery(id+"F0.wireOp",EDGE,"E4.5.0.2");var subQ339=makeQuery(id+"F0.imprint","INTERSECT",VERTEX,{"derivedFrom":[subQ338,subQ337]});var subQ341=makeQuery(id+"F0.imprint","IMPRINT",EDGE,{"disambiguationData":[TD([[subQ339,1.0]])],"derivedFrom":subQ338});var subQ348=sQuery(id+"F0.wireOp",EDGE,"E4.5.0.13");var subQ349=sQuery(id+"F0.wireOp",EDGE,"E4.5.0.9");var subQ352=sQuery(id+"F0.wireOp",EDGE,"E4.5.0.0");var subQ353=makeQuery(id+"F0.imprint","INTERSECT",VERTEX,{"derivedFrom":[subQ352,subQ349]});var subQ355=makeQuery(id+"F0.imprint","IMPRINT",EDGE,{"disambiguationData":[TD([[subQ353,1.0]])],"derivedFrom":subQ352});var subQ361=sQuery(id+"F0.wireOp",EDGE,"E4.4.0.7");var subQ364=makeQuery(id+"F0.imprint","IMPRINT",EDGE,{"derivedFrom":subQ361});var subQ365=sQuery(id+"F0.wireOp",EDGE,"E4.4.0.6");var subQ366=sQuery(id+"F0.wireOp",EDGE,"E4.4.0.2");var subQ367=makeQuery(id+"F0.imprint","INTERSECT",VERTEX,{"derivedFrom":[subQ366,subQ365]});var subQ369=makeQuery(id+"F0.imprint","IMPRINT",EDGE,{"disambiguationData":[TD([[subQ367,1.0]])],"derivedFrom":subQ366});var subQ376=sQuery(id+"F0.wireOp",EDGE,"E4.4.0.13");var subQ377=sQuery(id+"F0.wireOp",EDGE,"E4.4.0.9");var subQ380=sQuery(id+"F0.wireOp",EDGE,"E4.4.0.0");var subQ381=makeQuery(id+"F0.imprint","INTERSECT",VERTEX,{"derivedFrom":[subQ380,subQ377]});var subQ383=makeQuery(id+"F0.imprint","IMPRINT",EDGE,{"disambiguationData":[TD([[subQ381,1.0]])],"derivedFrom":subQ380});var subQ389=sQuery(id+"F0.wireOp",EDGE,"E4.3.0.7");var subQ392=makeQuery(id+"F0.imprint","IMPRINT",EDGE,{"derivedFrom":subQ389});var subQ393=sQuery(id+"F0.wireOp",EDGE,"E4.3.0.6");var subQ394=sQuery(id+"F0.wireOp",EDGE,"E4.3.0.2");var subQ395=makeQuery(id+"F0.imprint","INTERSECT",VERTEX,{"derivedFrom":[subQ394,subQ393]});var subQ397=makeQuery(id+"F0.imprint","IMPRINT",EDGE,{"disambiguationData":[TD([[subQ395,1.0]])],"derivedFrom":subQ394});var subQ404=sQuery(id+"F0.wireOp",EDGE,"E4.3.0.13");var subQ405=sQuery(id+"F0.wireOp",EDGE,"E4.3.0.9");var subQ408=sQuery(id+"F0.wireOp",EDGE,"E4.3.0.0");var subQ409=makeQuery(id+"F0.imprint","INTERSECT",VERTEX,{"derivedFrom":[subQ408,subQ405]});var subQ411=makeQuery(id+"F0.imprint","IMPRINT",EDGE,{"disambiguationData":[TD([[subQ409,1.0]])],"derivedFrom":subQ408});var subQ417=sQuery(id+"F0.wireOp",EDGE,"E4.2.0.7");var subQ420=makeQuery(id+"F0.imprint","IMPRINT",EDGE,{"derivedFrom":subQ417});var subQ421=sQuery(id+"F0.wireOp",EDGE,"E4.2.0.6");var subQ422=sQuery(id+"F0.wireOp",EDGE,"E4.2.0.2");var subQ423=makeQuery(id+"F0.imprint","INTERSECT",VERTEX,{"derivedFrom":[subQ422,subQ421]});var subQ425=makeQuery(id+"F0.imprint","IMPRINT",EDGE,{"disambiguationData":[TD([[subQ423,1.0]])],"derivedFrom":subQ422});var subQ432=sQuery(id+"F0.wireOp",EDGE,"E4.2.0.13");var subQ433=sQuery(id+"F0.wireOp",EDGE,"E4.2.0.9");var subQ436=sQuery(id+"F0.wireOp",EDGE,"E4.2.0.0");var subQ437=makeQuery(id+"F0.imprint","INTERSECT",VERTEX,{"derivedFrom":[subQ436,subQ433]});var subQ439=makeQuery(id+"F0.imprint","IMPRINT",EDGE,{"disambiguationData":[TD([[subQ437,1.0]])],"derivedFrom":subQ436});var subQ445=sQuery(id+"F0.wireOp",EDGE,"E4.1.0.7");var subQ448=makeQuery(id+"F0.imprint","IMPRINT",EDGE,{"derivedFrom":subQ445});var subQ449=sQuery(id+"F0.wireOp",EDGE,"E4.1.0.6");var subQ450=sQuery(id+"F0.wireOp",EDGE,"E4.1.0.2");var subQ451=makeQuery(id+"F0.imprint","INTERSECT",VERTEX,{"derivedFrom":[subQ450,subQ449]});var subQ453=makeQuery(id+"F0.imprint","IMPRINT",EDGE,{"disambiguationData":[TD([[subQ451,1.0]])],"derivedFrom":subQ450});var subQ460=sQuery(id+"F0.wireOp",EDGE,"E4.1.0.13");var subQ461=sQuery(id+"F0.wireOp",EDGE,"E4.1.0.9");var subQ464=sQuery(id+"F0.wireOp",EDGE,"E4.1.0.0");var subQ465=makeQuery(id+"F0.imprint","INTERSECT",VERTEX,{"derivedFrom":[subQ464,subQ461]});var subQ467=makeQuery(id+"F0.imprint","IMPRINT",EDGE,{"disambiguationData":[TD([[subQ465,1.0]])],"derivedFrom":subQ464});var subQ473=sQuery(id+"F0.wireOp",EDGE,"E3.right");var subQ476=makeQuery(id+"F0.imprint","IMPRINT",EDGE,{"derivedFrom":subQ473});var subQ477=sQuery(id+"F0.wireOp",EDGE,"E3.bottom");var subQ479=sQuery(id+"F0.wireOp",EDGE,"E2.top");var subQ485=sQuery(id+"F0.wireOp",EDGE,"E1.right");var subQ489=makeQuery(id+"F0.imprint","IMPRINT",EDGE,{"derivedFrom":subQ485});var subQ490=sQuery(id+"F0.wireOp",EDGE,"E1.bottom");var subQ492=sQuery(id+"F0.wireOp",EDGE,"E0.top");var subQ498=sQuery(id+"F0.wireOp",EDGE,"E4.17.0.7");var subQ499=sQuery(id+"F0.wireOp",EDGE,"E0.bottom");Q0=qUnion([makeQuery(id+"F0.imprint","IMPRINT",FACE,{"disambiguationData":[TD([[makeQuery(id+"F0.imprint","IMPRINT",EDGE,{"derivedFrom":subQ499}),-1.0]])]}),makeQuery(id+"F0.imprint","IMPRINT",FACE,{"disambiguationData":[TD([[makeQuery(id+"F0.imprint","IMPRINT",EDGE,{"derivedFrom":subQ498}),-1.0]])]}),makeQuery(id+"F0.imprint","IMPRINT",FACE,{"disambiguationData":[TD([[makeQuery(id+"F0.imprint","IMPRINT",EDGE,{"derivedFrom":subQ492}),1.0]])]}),makeQuery(id+"F0.imprint","IMPRINT",FACE,{"disambiguationData":[TD([[makeQuery(id+"F0.imprint","IMPRINT",EDGE,{"derivedFrom":subQ490}),1.0]])]}),makeQuery(id+"F0.imprint","IMPRINT",FACE,{"disambiguationData":[TD([[subQ489,-1.0]])]}),makeQuery(id+"F0.imprint","IMPRINT",FACE,{"disambiguationData":[TD([[makeQuery(id+"F0.imprint","IMPRINT",EDGE,{"derivedFrom":subQ479}),-1.0]])]}),makeQuery(id+"F0.imprint","IMPRINT",FACE,{"disambiguationData":[TD([[makeQuery(id+"F0.imprint","IMPRINT",EDGE,{"derivedFrom":subQ477}),-1.0]])]}),makeQuery(id+"F0.imprint","IMPRINT",FACE,{"disambiguationData":[TD([[subQ476,1.0]])]}),makeQuery(id+"F0.imprint","IMPRINT",FACE,{"disambiguationData":[TD([[subQ467,-1.0]])]}),makeQuery(id+"F0.imprint","IMPRINT",FACE,{"disambiguationData":[TD([[subQ467,1.0]])]}),makeQuery(id+"F0.imprint","IMPRINT",FACE,{"disambiguationData":[TD([[makeQuery(id+"F0.imprint","IMPRINT",EDGE,{"derivedFrom":subQ460}),1.0]])]}),makeQuery(id+"F0.imprint","IMPRINT",FACE,{"disambiguationData":[TD([[subQ453,1.0]])]}),makeQuery(id+"F0.imprint","IMPRINT",FACE,{"disambiguationData":[TD([[subQ448,-1.0]])]}),makeQuery(id+"F0.imprint","IMPRINT",FACE,{"disambiguationData":[TD([[subQ448,1.0]])]}),makeQuery(id+"F0.imprint","IMPRINT",FACE,{"disambiguationData":[TD([[subQ439,-1.0]])]}),makeQuery(id+"F0.imprint","IMPRINT",FACE,{"disambiguationData":[TD([[subQ439,1.0]])]}),makeQuery(id+"F0.imprint","IMPRINT",FACE,{"disambiguationData":[TD([[makeQuery(id+"F0.imprint","IMPRINT",EDGE,{"derivedFrom":subQ432}),1.0]])]}),makeQuery(id+"F0.imprint","IMPRINT",FACE,{"disambiguationData":[TD([[subQ425,1.0]])]}),makeQuery(id+"F0.imprint","IMPRINT",FACE,{"disambiguationData":[TD([[subQ420,-1.0]])]}),makeQuery(id+"F0.imprint","IMPRINT",FACE,{"disambiguationData":[TD([[subQ420,1.0]])]}),makeQuery(id+"F0.imprint","IMPRINT",FACE,{"disambiguationData":[TD([[subQ411,-1.0]])]}),makeQuery(id+"F0.imprint","IMPRINT",FACE,{"disambiguationData":[TD([[subQ411,1.0]])]}),makeQuery(id+"F0.imprint","IMPRINT",FACE,{"disambiguationData":[TD([[makeQuery(id+"F0.imprint","IMPRINT",EDGE,{"derivedFrom":subQ404}),1.0]])]}),makeQuery(id+"F0.imprint","IMPRINT",FACE,{"disambiguationData":[TD([[subQ397,1.0]])]}),makeQuery(id+"F0.imprint","IMPRINT",FACE,{"disambiguationData":[TD([[subQ392,-1.0]])]}),makeQuery(id+"F0.imprint","IMPRINT",FACE,{"disambiguationData":[TD([[subQ392,1.0]])]}),makeQuery(id+"F0.imprint","IMPRINT",FACE,{"disambiguationData":[TD([[subQ383,-1.0]])]}),makeQuery(id+"F0.imprint","IMPRINT",FACE,{"disambiguationData":[TD([[subQ383,1.0]])]}),makeQuery(id+"F0.imprint","IMPRINT",FACE,{"disambiguationData":[TD([[makeQuery(id+"F0.imprint","IMPRINT",EDGE,{"derivedFrom":subQ376}),1.0]])]}),makeQuery(id+"F0.imprint","IMPRINT",FACE,{"disambiguationData":[TD([[subQ369,1.0]])]}),makeQuery(id+"F0.imprint","IMPRINT",FACE,{"disambiguationData":[TD([[subQ364,-1.0]])]}),makeQuery(id+"F0.imprint","IMPRINT",FACE,{"disambiguationData":[TD([[subQ364,1.0]])]}),makeQuery(id+"F0.imprint","IMPRINT",FACE,{"disambiguationData":[TD([[subQ355,-1.0]])]}),makeQuery(id+"F0.imprint","IMPRINT",FACE,{"disambiguationData":[TD([[subQ355,1.0]])]}),makeQuery(id+"F0.imprint","IMPRINT",FACE,{"disambiguationData":[TD([[makeQuery(id+"F0.imprint","IMPRINT",EDGE,{"derivedFrom":subQ348}),1.0]])]}),makeQuery(id+"F0.imprint","IMPRINT",FACE,{"disambiguationData":[TD([[subQ341,1.0]])]}),makeQuery(id+"F0.imprint","IMPRINT",FACE,{"disambiguationData":[TD([[subQ336,-1.0]])]}),makeQuery(id+"F0.imprint","IMPRINT",FACE,{"disambiguationData":[TD([[subQ336,1.0]])]}),makeQuery(id+"F0.imprint","IMPRINT",FACE,{"disambiguationData":[TD([[subQ327,-1.0]])]}),makeQuery(id+"F0.imprint","IMPRINT",FACE,{"disambiguationData":[TD([[subQ327,1.0]])]}),makeQuery(id+"F0.imprint","IMPRINT",FACE,{"disambiguationData":[TD([[makeQuery(id+"F0.imprint","IMPRINT",EDGE,{"derivedFrom":subQ320}),1.0]])]}),makeQuery(id+"F0.imprint","IMPRINT",FACE,{"disambiguationData":[TD([[subQ313,1.0]])]}),makeQuery(id+"F0.imprint","IMPRINT",FACE,{"disambiguationData":[TD([[subQ308,-1.0]])]}),makeQuery(id+"F0.imprint","IMPRINT",FACE,{"disambiguationData":[TD([[subQ308,1.0]])]}),makeQuery(id+"F0.imprint","IMPRINT",FACE,{"disambiguationData":[TD([[subQ299,-1.0]])]}),makeQuery(id+"F0.imprint","IMPRINT",FACE,{"disambiguationData":[TD([[subQ299,1.0]])]}),makeQuery(id+"F0.imprint","IMPRINT",FACE,{"disambiguationData":[TD([[makeQuery(id+"F0.imprint","IMPRINT",EDGE,{"derivedFrom":subQ292}),1.0]])]}),makeQuery(id+"F0.imprint","IMPRINT",FACE,{"disambiguationData":[TD([[subQ285,1.0]])]}),makeQuery(id+"F0.imprint","IMPRINT",FACE,{"disambiguationData":[TD([[subQ280,-1.0]])]}),makeQuery(id+"F0.imprint","IMPRINT",FACE,{"disambiguationData":[TD([[subQ280,1.0]])]}),makeQuery(id+"F0.imprint","IMPRINT",FACE,{"disambiguationData":[TD([[subQ271,-1.0]])]}),makeQuery(id+"F0.imprint","IMPRINT",FACE,{"disambiguationData":[TD([[subQ271,1.0]])]}),makeQuery(id+"F0.imprint","IMPRINT",FACE,{"disambiguationData":[TD([[makeQuery(id+"F0.imprint","IMPRINT",EDGE,{"derivedFrom":subQ264}),1.0]])]}),makeQuery(id+"F0.imprint","IMPRINT",FACE,{"disambiguationData":[TD([[subQ257,1.0]])]}),makeQuery(id+"F0.imprint","IMPRINT",FACE,{"disambiguationData":[TD([[subQ252,-1.0]])]}),makeQuery(id+"F0.imprint","IMPRINT",FACE,{"disambiguationData":[TD([[subQ252,1.0]])]}),makeQuery(id+"F0.imprint","IMPRINT",FACE,{"disambiguationData":[TD([[subQ243,-1.0]])]}),makeQuery(id+"F0.imprint","IMPRINT",FACE,{"disambiguationData":[TD([[subQ243,1.0]])]}),makeQuery(id+"F0.imprint","IMPRINT",FACE,{"disambiguationData":[TD([[makeQuery(id+"F0.imprint","IMPRINT",EDGE,{"derivedFrom":subQ236}),1.0]])]}),makeQuery(id+"F0.imprint","IMPRINT",FACE,{"disambiguationData":[TD([[subQ229,1.0]])]}),makeQuery(id+"F0.imprint","IMPRINT",FACE,{"disambiguationData":[TD([[subQ224,-1.0]])]}),makeQuery(id+"F0.imprint","IMPRINT",FACE,{"disambiguationData":[TD([[subQ224,1.0]])]}),makeQuery(id+"F0.imprint","IMPRINT",FACE,{"disambiguationData":[TD([[subQ215,-1.0]])]}),makeQuery(id+"F0.imprint","IMPRINT",FACE,{"disambiguationData":[TD([[subQ215,1.0]])]}),makeQuery(id+"F0.imprint","IMPRINT",FACE,{"disambiguationData":[TD([[makeQuery(id+"F0.imprint","IMPRINT",EDGE,{"derivedFrom":subQ208}),1.0]])]}),makeQuery(id+"F0.imprint","IMPRINT",FACE,{"disambiguationData":[TD([[subQ201,1.0]])]}),makeQuery(id+"F0.imprint","IMPRINT",FACE,{"disambiguationData":[TD([[subQ196,-1.0]])]}),makeQuery(id+"F0.imprint","IMPRINT",FACE,{"disambiguationData":[TD([[subQ196,1.0]])]}),makeQuery(id+"F0.imprint","IMPRINT",FACE,{"disambiguationData":[TD([[subQ187,-1.0]])]}),makeQuery(id+"F0.imprint","IMPRINT",FACE,{"disambiguationData":[TD([[subQ187,1.0]])]}),makeQuery(id+"F0.imprint","IMPRINT",FACE,{"disambiguationData":[TD([[makeQuery(id+"F0.imprint","IMPRINT",EDGE,{"derivedFrom":subQ180}),1.0]])]}),makeQuery(id+"F0.imprint","IMPRINT",FACE,{"disambiguationData":[TD([[subQ173,1.0]])]}),makeQuery(id+"F0.imprint","IMPRINT",FACE,{"disambiguationData":[TD([[subQ168,-1.0]])]}),makeQuery(id+"F0.imprint","IMPRINT",FACE,{"disambiguationData":[TD([[subQ168,1.0]])]}),makeQuery(id+"F0.imprint","IMPRINT",FACE,{"disambiguationData":[TD([[subQ159,-1.0]])]}),makeQuery(id+"F0.imprint","IMPRINT",FACE,{"disambiguationData":[TD([[subQ159,1.0]])]}),makeQuery(id+"F0.imprint","IMPRINT",FACE,{"disambiguationData":[TD([[makeQuery(id+"F0.imprint","IMPRINT",EDGE,{"derivedFrom":subQ152}),1.0]])]}),makeQuery(id+"F0.imprint","IMPRINT",FACE,{"disambiguationData":[TD([[subQ145,1.0]])]}),makeQuery(id+"F0.imprint","IMPRINT",FACE,{"disambiguationData":[TD([[subQ140,-1.0]])]}),makeQuery(id+"F0.imprint","IMPRINT",FACE,{"disambiguationData":[TD([[subQ140,1.0]])]}),makeQuery(id+"F0.imprint","IMPRINT",FACE,{"disambiguationData":[TD([[subQ131,-1.0]])]}),makeQuery(id+"F0.imprint","IMPRINT",FACE,{"disambiguationData":[TD([[subQ131,1.0]])]}),makeQuery(id+"F0.imprint","IMPRINT",FACE,{"disambiguationData":[TD([[makeQuery(id+"F0.imprint","IMPRINT",EDGE,{"derivedFrom":subQ124}),1.0]])]}),makeQuery(id+"F0.imprint","IMPRINT",FACE,{"disambiguationData":[TD([[subQ117,1.0]])]}),makeQuery(id+"F0.imprint","IMPRINT",FACE,{"disambiguationData":[TD([[subQ112,-1.0]])]}),makeQuery(id+"F0.imprint","IMPRINT",FACE,{"disambiguationData":[TD([[subQ112,1.0]])]}),makeQuery(id+"F0.imprint","IMPRINT",FACE,{"disambiguationData":[TD([[subQ103,-1.0]])]}),makeQuery(id+"F0.imprint","IMPRINT",FACE,{"disambiguationData":[TD([[subQ103,1.0]])]}),makeQuery(id+"F0.imprint","IMPRINT",FACE,{"disambiguationData":[TD([[makeQuery(id+"F0.imprint","IMPRINT",EDGE,{"derivedFrom":subQ96}),1.0]])]}),makeQuery(id+"F0.imprint","IMPRINT",FACE,{"disambiguationData":[TD([[subQ89,1.0]])]}),makeQuery(id+"F0.imprint","IMPRINT",FACE,{"disambiguationData":[TD([[subQ84,-1.0]])]}),makeQuery(id+"F0.imprint","IMPRINT",FACE,{"disambiguationData":[TD([[subQ84,1.0]])]}),makeQuery(id+"F0.imprint","IMPRINT",FACE,{"disambiguationData":[TD([[subQ75,-1.0]])]}),makeQuery(id+"F0.imprint","IMPRINT",FACE,{"disambiguationData":[TD([[subQ75,1.0]])]}),makeQuery(id+"F0.imprint","IMPRINT",FACE,{"disambiguationData":[TD([[makeQuery(id+"F0.imprint","IMPRINT",EDGE,{"derivedFrom":subQ68}),1.0]])]}),makeQuery(id+"F0.imprint","IMPRINT",FACE,{"disambiguationData":[TD([[subQ61,1.0]])]}),makeQuery(id+"F0.imprint","IMPRINT",FACE,{"disambiguationData":[TD([[subQ56,-1.0]])]}),makeQuery(id+"F0.imprint","IMPRINT",FACE,{"disambiguationData":[TD([[subQ56,1.0]])]}),makeQuery(id+"F0.imprint","IMPRINT",FACE,{"disambiguationData":[TD([[subQ47,-1.0]])]}),makeQuery(id+"F0.imprint","IMPRINT",FACE,{"disambiguationData":[TD([[subQ47,1.0]])]}),makeQuery(id+"F0.imprint","IMPRINT",FACE,{"disambiguationData":[TD([[makeQuery(id+"F0.imprint","IMPRINT",EDGE,{"derivedFrom":subQ40}),1.0]])]}),makeQuery(id+"F0.imprint","IMPRINT",FACE,{"disambiguationData":[TD([[subQ33,1.0]])]}),makeQuery(id+"F0.imprint","IMPRINT",FACE,{"disambiguationData":[TD([[subQ28,-1.0]])]}),makeQuery(id+"F0.imprint","IMPRINT",FACE,{"disambiguationData":[TD([[subQ28,1.0]])]}),makeQuery(id+"F0.imprint","IMPRINT",FACE,{"disambiguationData":[TD([[subQ19,-1.0]])]}),makeQuery(id+"F0.imprint","IMPRINT",FACE,{"disambiguationData":[TD([[subQ19,1.0]])]}),makeQuery(id+"F0.imprint","IMPRINT",FACE,{"disambiguationData":[TD([[makeQuery(id+"F0.imprint","IMPRINT",EDGE,{"derivedFrom":subQ12}),1.0]])]}),makeQuery(id+"F0.imprint","IMPRINT",FACE,{"disambiguationData":[TD([[subQ5,1.0]])]})]);}
            extrude(context, id + "F1", {"entities" : qUnion([Q0]), "depth" : 0.4 * mm, "offsetDistance" : 25 * mm});
        }
    });
